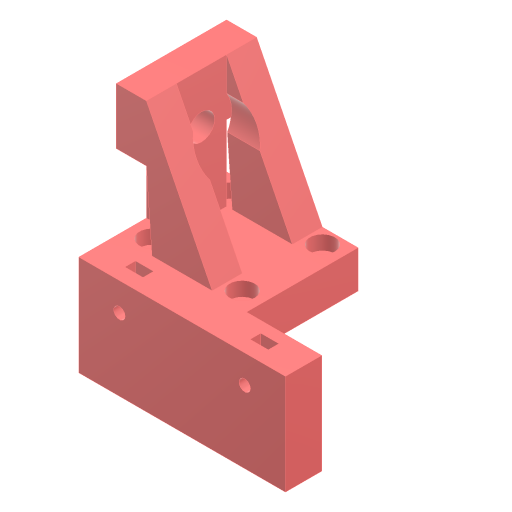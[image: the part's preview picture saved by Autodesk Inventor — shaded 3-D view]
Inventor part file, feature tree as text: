
AUTODESK INVENTOR PART (.ipt)
format: ipt  version: 2024.3 (Build 283343000, 343)  size: 522,240 bytes
history: native  units: mm
features: sketch x13, projected_geometry x10, extrude x8, hole x5, mirror x1
ambient origin geometry x8: Origin, YZ Plane, XZ Plane, XY Plane, X Axis, Y Axis, Z Axis, Center Point
bodies: Solid1 (feature_tree)
feature tree (37):
  extrude  "Extrusion1"  Depth=52.5mm
  hole  "Hole1"  [1 undecoded]
  hole  "Hole2"  [1 undecoded]
  extrude  "Extrusion2"  Depth=12.0mm
  extrude  "Extrusion3"  Depth=6.0mm
  hole  "Hole3"  [1 undecoded]
  mirror  "Mirror1"
  extrude  "Extrusion4"  Depth=30.0mm
  extrude  "Extrusion5"  Depth=6.0mm
  extrude  "Extrusion6"  Depth=5.7mm
  extrude  "Extrusion7"  Depth=15.0mm TaperAngle=0.0deg
  hole  "Hole4"  [1 undecoded]
  extrude  "Extrusion8"  Depth=30.0mm TaperAngle=0.0deg
  hole  "Hole5"  [1 undecoded]
  sketch  "Sketch1"  dims[d0=44.0mm d1=52.5mm]
  sketch  "Sketch2"  dims[d2=67.5mm d3=0.0mm d4=32.0mm]
  sketch  "Sketch3"  dims[d5=36.0mm]
  projected_geometry  "Projected Loop1"
  sketch  "Sketch4"  dims[d6=5.6mm d7=6.0mm d8=4.0mm d9=2.0mm d10=90.0deg d11=8.0mm d12=20.594885mm d13=47.5mm]
  projected_geometry  "Projected Loop2"
  sketch  "Sketch5"  dims[d14=10.5mm d15=6.0mm d16=4.0mm d17=2.0mm d18=90.0deg d19=8.0mm d20=20.594885mm d21=12.0mm]
  projected_geometry  "Projected Loop3"
  sketch  "Sketch6"  dims[d22=6.0mm d23=6.0mm]
  projected_geometry  "Projected Loop4"
  sketch  "Sketch7"  dims[d24=6.0mm d25=52.5mm d26=0.0mm]
  sketch  "Sketch8"  dims[d27=30.0mm d28=36.0mm]
  projected_geometry  "Projected Loop5"
  sketch  "Sketch9"  dims[d29=6.0mm d30=6.0mm]
  projected_geometry  "Projected Loop6"
  sketch  "Sketch10"  dims[d31=52.5mm d32=0.0mm]
  projected_geometry  "Projected Loop7"
  sketch  "Sketch11"  dims[d33=5.5mm d34=6.0mm d35=10.0mm d36=5.7mm d37=90.0deg d38=8.0mm d39=20.594885mm d40=24.0mm]
  projected_geometry  "Projected Loop8"
  sketch  "Sketch12"  dims[d41=0.0mm d42=0.0mm d43=15.0mm d44=0.0mm]
  sketch  "Sketch13"  dims[d45=14.5mm d46=25.0mm d47=0.0mm d48=30.0mm d49=0.0mm d50=50.0mm d51=25.0mm d52=5.0mm d53=33.8mm d54=4.6mm d55=6.0mm d56=10.0mm d57=5.7mm d58=90.0deg d59=10.0mm d60=0.0mm d61=7.2mm d62=4.2mm d63=0.0mm d64=4.6mm d65=6.0mm d66=4.0mm d67=2.0mm d68=90.0deg d69=5.0mm d70=0.0mm]
  projected_geometry  "Projected Loop9"
  projected_geometry  "Projected Loop10"
note: 5 required parameter values undecoded (feature->parameter linkage not recoverable at this tier; creation-order binding heuristic only, values carry confidence <= 0.55)
